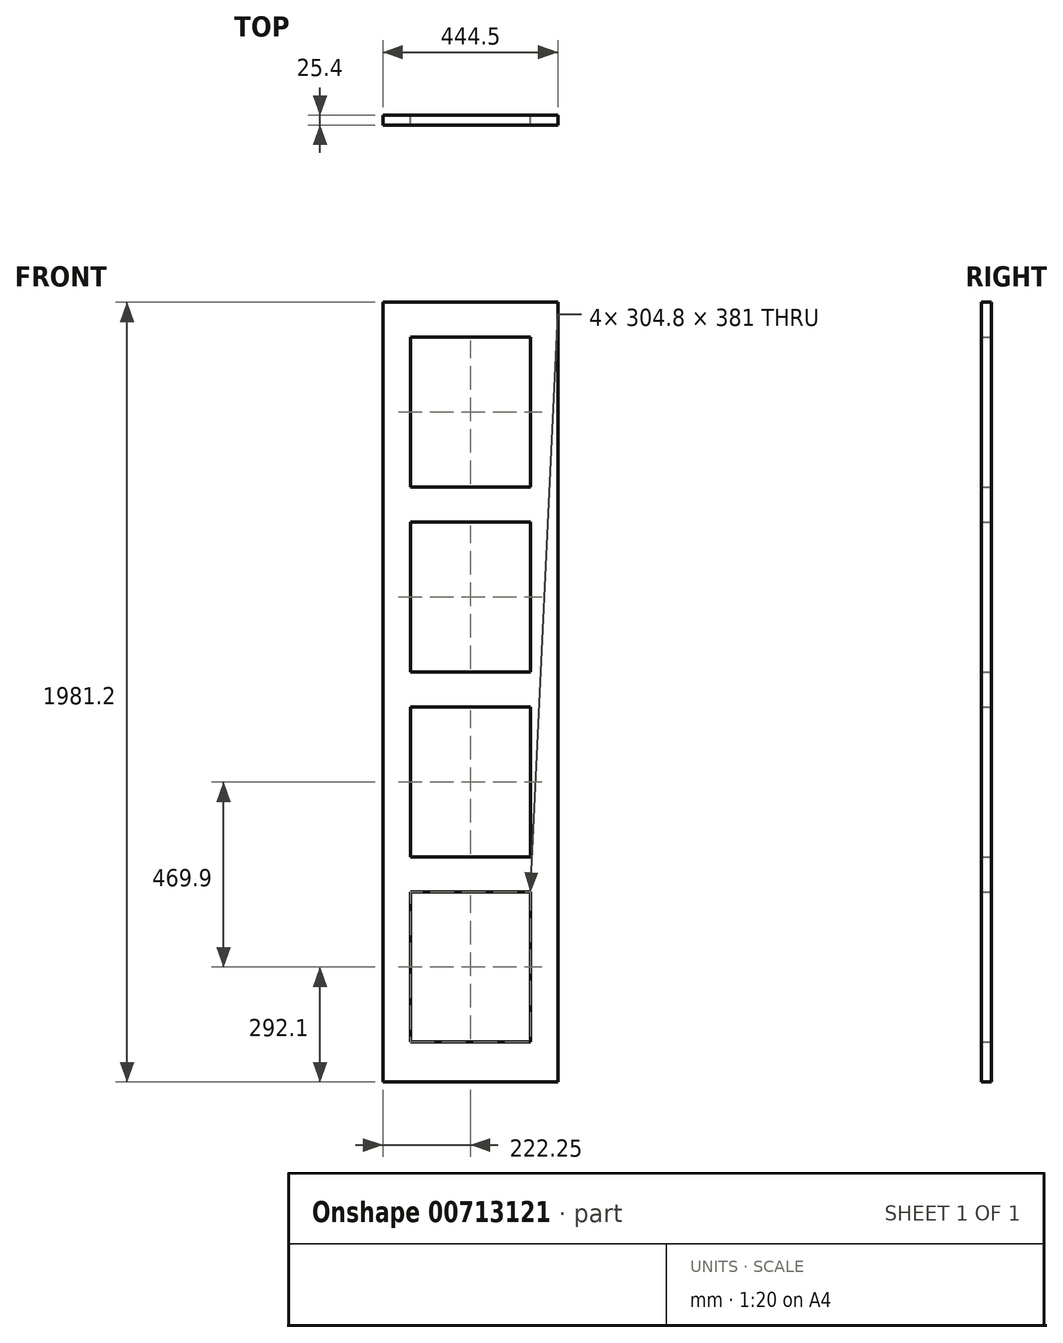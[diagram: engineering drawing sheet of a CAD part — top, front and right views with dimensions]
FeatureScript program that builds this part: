
annotation { "Feature Type Name" : "Feature", "Feature Type Description" : "" }
export const myFeature = defineFeature(function(context is Context, id is Id, definition is map)
    precondition{}
    {
        {
            var Q0;
            Q0=qCreatedBy(makeId("Front.planeOp"),FACE);
            var sketch = newSketch(context, id + "F0", { "sketchPlane" : qUnion([Q0])});
            skLineSegment(sketch, "E0.bottom", {"start": v(-222.25, 1016) * mm, "end": v(222.25, 1016) * mm});
            skLineSegment(sketch, "E0.top", {"start": v(-222.25, -965.2) * mm, "end": v(222.25, -965.2) * mm});
            skLineSegment(sketch, "E0.left", {"start": v(-222.25, 1016) * mm, "end": v(-222.25, -965.2) * mm});
            skLineSegment(sketch, "E0.right", {"start": v(222.25, 1016) * mm, "end": v(222.25, -965.2) * mm});
            skPoint(sketch, "E1.middle", {"position": v(0, 711.2) * mm});
            skLineSegment(sketch, "E2.0", {"start": v(-152.4, 927.1) * mm, "end": v(152.4, 927.1) * mm});
            skLineSegment(sketch, "E2.1", {"start": v(-152.4, 546.1) * mm, "end": v(-152.4, 927.1) * mm});
            skLineSegment(sketch, "E2.2", {"start": v(-152.4, 546.1) * mm, "end": v(152.4, 546.1) * mm});
            skLineSegment(sketch, "E2.3", {"start": v(152.4, 546.1) * mm, "end": v(152.4, 927.1) * mm});
            skLineSegment(sketch, "E3.0.1.0", {"start": v(152.4, 76.2) * mm, "end": v(152.4, 457.2) * mm});
            skPoint(sketch, "E3.0.1.1", {"position": v(0, 241.3) * mm});
            skLineSegment(sketch, "E3.0.1.2", {"start": v(-152.4, 76.2) * mm, "end": v(152.4, 76.2) * mm});
            skLineSegment(sketch, "E3.0.1.3", {"start": v(-152.4, 76.2) * mm, "end": v(-152.4, 457.2) * mm});
            skLineSegment(sketch, "E3.0.1.4", {"start": v(-152.4, 457.2) * mm, "end": v(152.4, 457.2) * mm});
            skLineSegment(sketch, "E3.0.2.0", {"start": v(152.4, -393.7) * mm, "end": v(152.4, -12.7) * mm});
            skPoint(sketch, "E3.0.2.1", {"position": v(0, -228.6) * mm});
            skLineSegment(sketch, "E3.0.2.2", {"start": v(-152.4, -393.7) * mm, "end": v(152.4, -393.7) * mm});
            skLineSegment(sketch, "E3.0.2.3", {"start": v(-152.4, -393.7) * mm, "end": v(-152.4, -12.7) * mm});
            skLineSegment(sketch, "E3.0.2.4", {"start": v(-152.4, -12.7) * mm, "end": v(152.4, -12.7) * mm});
            skLineSegment(sketch, "E3.0.3.0", {"start": v(152.4, -863.6) * mm, "end": v(152.4, -482.6) * mm});
            skPoint(sketch, "E3.0.3.1", {"position": v(0, -698.5) * mm});
            skLineSegment(sketch, "E3.0.3.2", {"start": v(-152.4, -863.6) * mm, "end": v(152.4, -863.6) * mm});
            skLineSegment(sketch, "E3.0.3.3", {"start": v(-152.4, -863.6) * mm, "end": v(-152.4, -482.6) * mm});
            skLineSegment(sketch, "E3.0.3.4", {"start": v(-152.4, -482.6) * mm, "end": v(152.4, -482.6) * mm});
            skLineSegment(sketch, "E3.direction1", {"start": v(-152.4, 546.1) * mm, "end": v(-127, 546.1) * mm, "construction": true});
            skLineSegment(sketch, "E3.direction2", {"start": v(-152.4, 546.1) * mm, "end": v(-152.4, 76.2) * mm, "construction": true});
            skSolve(sketch);
        }
        {
            var Q0;
            Q0=makeQuery(id+"F0.imprint","IMPRINT",FACE,{"disambiguationData":[TD([[makeQuery(id+"F0.imprint","IMPRINT",EDGE,{"derivedFrom":sQuery(id+"F0.wireOp",EDGE,"E0.bottom")}),-1.0]])]});
            extrude(context, id + "F1", {"entities" : qUnion([Q0]), "depth" : 25.4 * mm, "offsetDistance" : 25.4 * mm});
        }
    });
